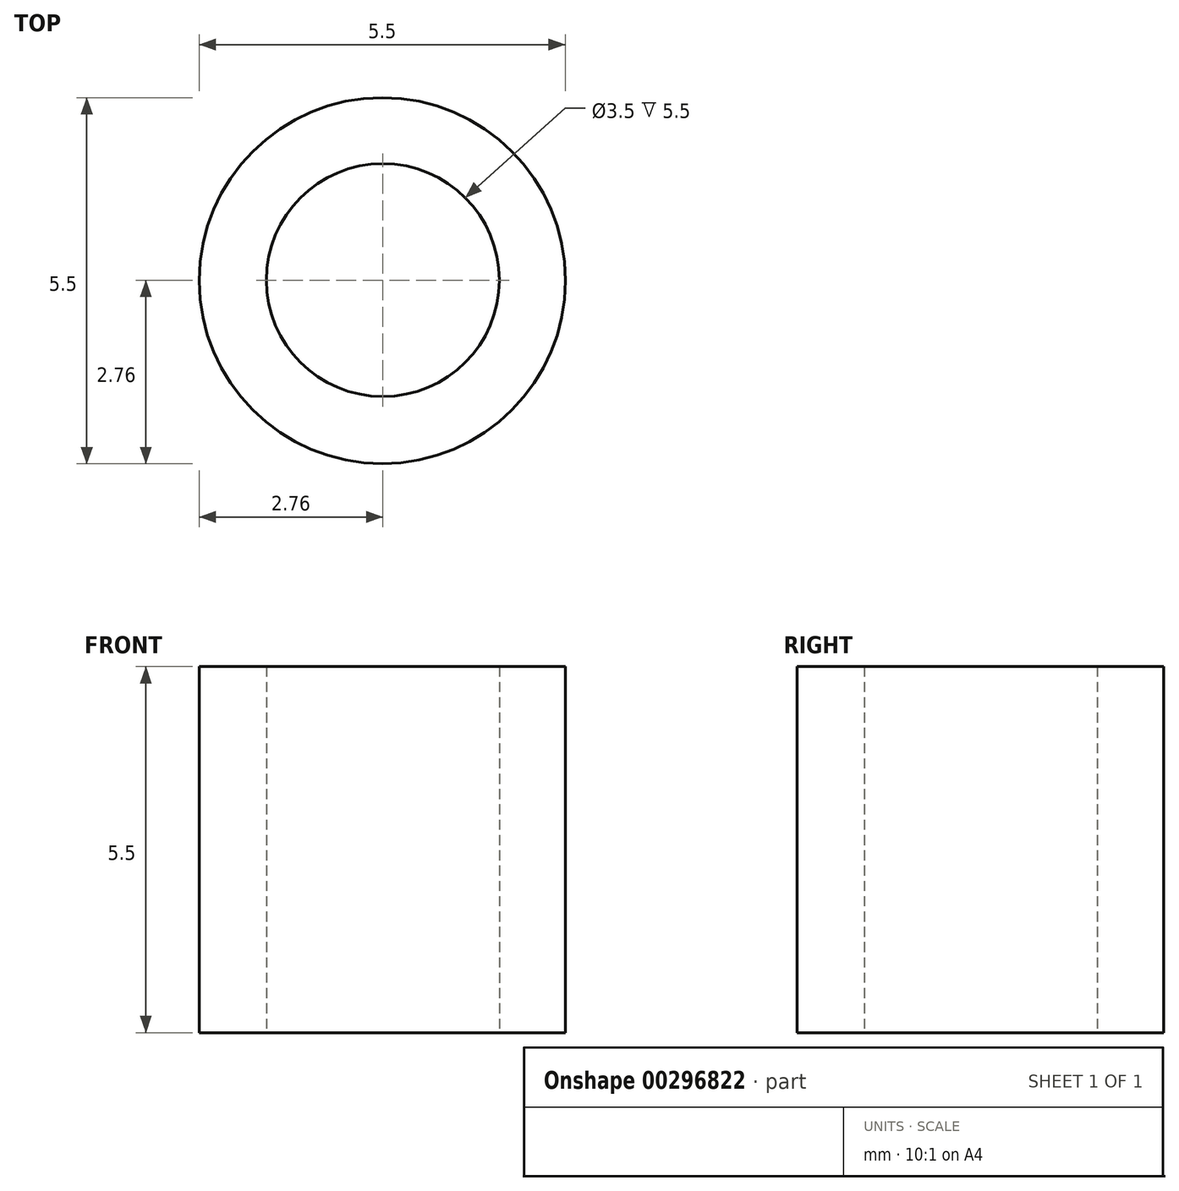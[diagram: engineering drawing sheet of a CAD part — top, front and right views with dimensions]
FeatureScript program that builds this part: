
annotation { "Feature Type Name" : "Feature", "Feature Type Description" : "" }
export const myFeature = defineFeature(function(context is Context, id is Id, definition is map)
    precondition{}
    {
        {
            var Q0;
            Q0=qCreatedBy(makeId("Top.planeOp"),FACE);
            var sketch = newSketch(context, id + "F0", { "sketchPlane" : qUnion([Q0])});
            skCircle(sketch, "E0", {"center": v(0, 0) * mm, "radius": 1.75 * mm});
            skCircle(sketch, "E1", {"center": v(0, 0) * mm, "radius": 2.75 * mm});
            skSolve(sketch);
        }
        {
            var Q0;
            Q0 = qSketchRegion(id + "F0", true);
            var Q1;
            Q1=makeQuery(id+"F0.imprint","IMPRINT",FACE,{"disambiguationData":[TD([[makeQuery(id+"F0.imprint","IMPRINT",EDGE,{"derivedFrom":sQuery(id+"F0.wireOp",EDGE,"E0")}),-1.0]])]});
            extrude(context, id + "F1", {"entities" : qUnion([Q0, Q1]), "depth" : 5.5 * mm});
        }
    });
